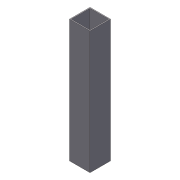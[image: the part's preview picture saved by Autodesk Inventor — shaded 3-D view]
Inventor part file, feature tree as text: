
AUTODESK INVENTOR PART (.ipt)
format: ipt  version: 2012 (Build 160160000, 160)  size: 75,776 bytes
history: native  units: in
note: dims shown in document units (in); Inventor stores cm internally (conversion verified against a paired STEP export)
features: extrude x1, shell x1, sketch x1
ambient origin geometry x8: Origin, YZ Plane, XZ Plane, XY Plane, X Axis, Y Axis, Z Axis, Center Point
bodies: Solid1 (feature_tree)
feature tree (3):
  extrude  "Extrusion1"  Depth=18.0in
  shell  "Shell1"  Thickness=3.0in
  sketch  "Sketch1"  dims[d0=3.0in d1=18.0in d2=3.0in d3=0.0in d4=0.125in]
